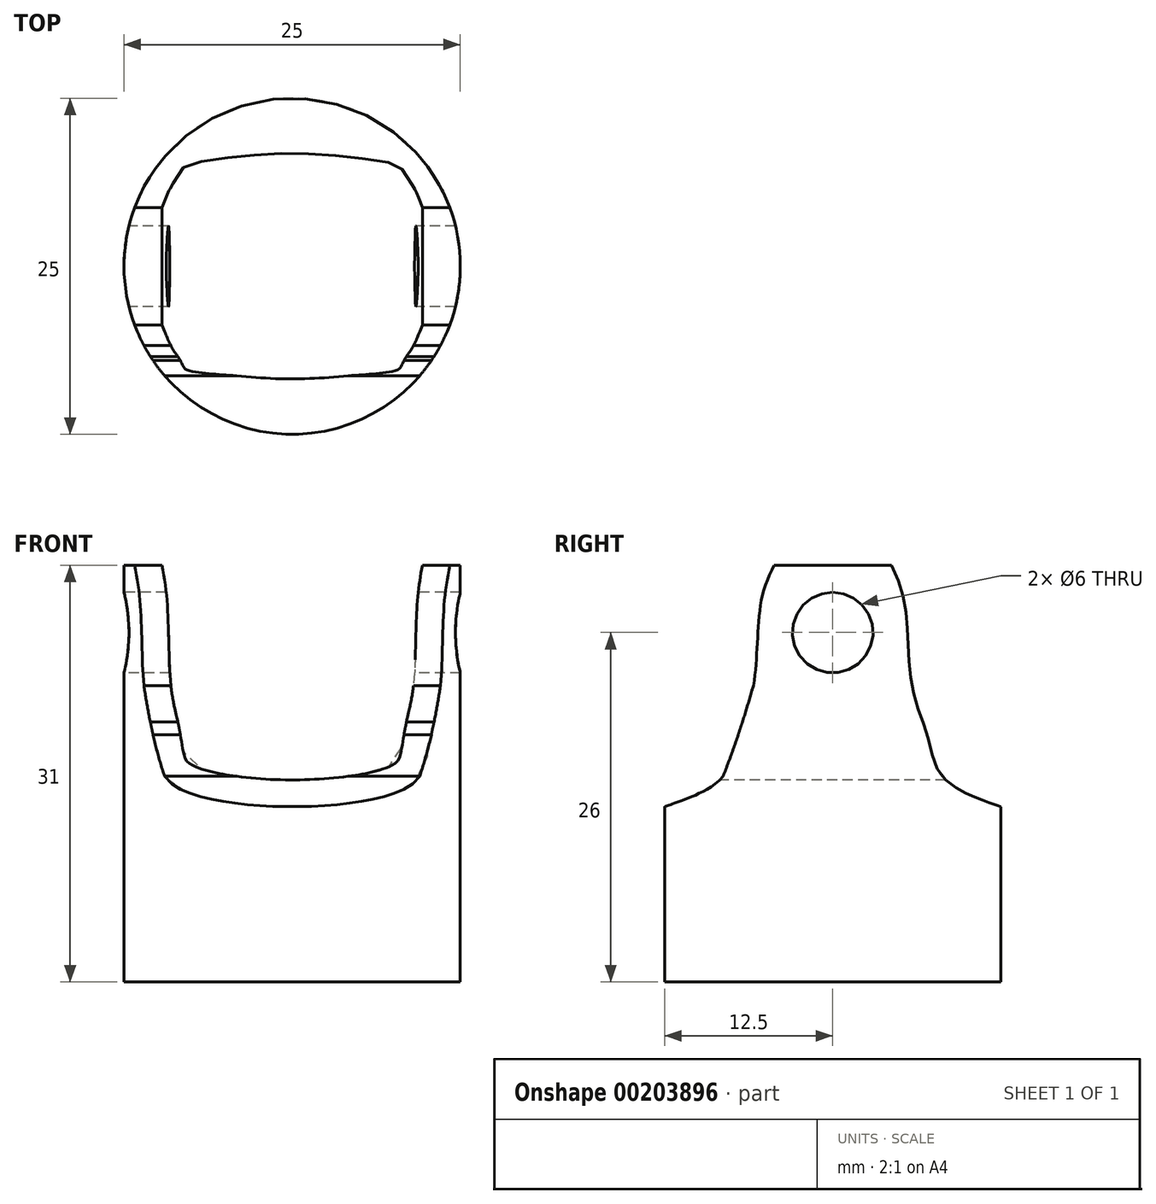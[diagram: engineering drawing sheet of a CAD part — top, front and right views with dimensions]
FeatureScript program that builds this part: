
annotation { "Feature Type Name" : "Feature", "Feature Type Description" : "" }
export const myFeature = defineFeature(function(context is Context, id is Id, definition is map)
    precondition{}
    {
        {
            var Q0;
            Q0=qCreatedBy(makeId("Top.planeOp"),FACE);
            var sketch = newSketch(context, id + "F0", { "sketchPlane" : qUnion([Q0])});
            skCircle(sketch, "E0", {"center": v(0, 0) * mm, "radius": 12.5 * mm});
            skSolve(sketch);
        }
        {
            var Q0;
            Q0=makeQuery(id+"F0.imprint","IMPRINT",FACE,{"disambiguationData":[TD([[makeQuery(id+"F0.imprint","IMPRINT",EDGE,{"derivedFrom":sQuery(id+"F0.wireOp",EDGE,"E0")}),1.0]])]});
            extrude(context, id + "F1", {"entities" : qUnion([Q0]), "depth" : 13 * mm});
        }
        {
            var Q0;
            Q0=makeQuery(id+"F1.opExtrude","CAP_FACE",FACE,{"disambiguationData":[OSD([sQuery(id+"F0.wireOp",EDGE,"E0")])],"isStart":false});
            extrude(context, id + "F2", {"entities" : qUnion([Q0]), "operationType" : NewBodyOperationType.ADD, "depth" : 18 * mm});
        }
        {
            var Q0;
            Q0=qCreatedBy(makeId("Right.planeOp"),FACE);
            var sketch = newSketch(context, id + "F3", { "sketchPlane" : qUnion([Q0])});
            skCircle(sketch, "E1", {"center": v(0, 26) * mm, "radius": 3 * mm});
            skLineSegment(sketch, "E2", {"start": v(-12.63, 13) * mm, "end": v(12.63, 13) * mm});
            skFitSpline(sketch, "E3", {"points": [v(-12.63, 13) * mm, v(-8.14, 15.3) * mm, v(-7.02, 18.39) * mm, v(-5.9, 22.04) * mm, v(-5.33, 28.22) * mm, v(-4.21, 31.3) * mm], "startDerivative": vector(24.86, 8.48) * mm, "endDerivative": vector(7.63, 15.3) * mm});
            skFitSpline(sketch, "E4", {"points": [v(-5.9, 22.04) * mm, v(-7.02, 18.39) * mm, v(-8.14, 15.3) * mm], "startDerivative": vector(-2.12, -7.2) * mm, "endDerivative": vector(-2.37, -6.27) * mm});
            skFitSpline(sketch, "E5.MirrorCS", {"points": [v(12.63, 13) * mm, v(8.14, 15.3) * mm, v(7.02, 18.39) * mm, v(5.9, 22.04) * mm, v(5.33, 28.22) * mm, v(4.21, 31.3) * mm], "startDerivative": vector(-24.86, 8.48) * mm, "endDerivative": vector(-7.63, 15.3) * mm});
            skFitSpline(sketch, "E6.MirrorCS", {"points": [v(12.63, 13) * mm, v(8.14, 15.3) * mm, v(7.02, 18.39) * mm, v(5.9, 22.04) * mm, v(5.33, 28.22) * mm, v(4.21, 31.3) * mm], "startDerivative": vector(-24.86, 8.48) * mm, "endDerivative": vector(-7.63, 15.3) * mm});
            skLineSegment(sketch, "E7", {"start": v(-4.21, 31.3) * mm, "end": v(4.21, 31.3) * mm});
            skLineSegment(sketch, "E8", {"start": v(-12.5, 0) * mm, "end": v(-12.5, 31) * mm});
            skLineSegment(sketch, "E9", {"start": v(12.5, 31) * mm, "end": v(12.5, 0) * mm});
            skLineSegment(sketch, "E10", {"start": v(-12.5, 0) * mm, "end": v(12.5, 0) * mm});
            skSolve(sketch);
        }
        {
            var Q0;
            Q0 = qSketchRegion(id + "F3", true);
            extrude(context, id + "F4", {"entities" : qUnion([Q0]), "operationType" : NewBodyOperationType.INTERSECT, "depth" : 25 * mm, "hasSecondDirection" : true, "secondDirectionOppositeDirection" : true, "secondDirectionDepth" : 25 * mm});
        }
        {
            var Q0;
            Q0=qCreatedBy(makeId("Front.planeOp"),FACE);
            var sketch = newSketch(context, id + "F5", { "sketchPlane" : qUnion([Q0])});
            skFitSpline(sketch, "E11.0", {"points": [v(-11.71, 31) * mm, v(-11.62, 30.5) * mm, v(-11.48, 29.74) * mm, v(-11.34, 28.68) * mm, v(-11.27, 27.86) * mm, v(-11.23, 27.02) * mm, v(-11.2, 25.9) * mm, v(-11.16, 24.47) * mm, v(-11.1, 23.06) * mm, v(-11.02, 21.95) * mm, v(-10.91, 21.12) * mm, v(-10.76, 20.31) * mm, v(-10.59, 19.5) * mm, v(-10.43, 18.84) * mm, v(-10.32, 18.3) * mm, v(-10.23, 17.74) * mm, v(-10.12, 17.03) * mm, v(-9.97, 16.35) * mm, v(-9.8, 15.85) * mm, v(-9.62, 15.5) * mm, v(-9.42, 15.2) * mm, v(-9.1, 14.86) * mm, v(-8.66, 14.52) * mm, v(-8.06, 14.2) * mm, v(-7.4, 13.96) * mm, v(-6.72, 13.76) * mm, v(-6, 13.59) * mm, v(-5.23, 13.44) * mm, v(-4.44, 13.32) * mm, v(-3.63, 13.23) * mm, v(-2.8, 13.15) * mm, v(-1.95, 13.1) * mm, v(-1.1, 13.06) * mm, v(0.05, 13.04) * mm, v(1.19, 13.06) * mm, v(2.33, 13.12) * mm, v(3.45, 13.2) * mm, v(4.53, 13.33) * mm, v(5.56, 13.5) * mm, v(6.32, 13.66) * mm, v(7.03, 13.84) * mm, v(7.7, 14.06) * mm, v(8.33, 14.34) * mm, v(8.81, 14.63) * mm, v(9.16, 14.92) * mm, v(9.4, 15.17) * mm, v(9.6, 15.46) * mm, v(9.77, 15.8) * mm, v(9.9, 16.18) * mm, v(10.05, 16.7) * mm, v(10.18, 17.4) * mm, v(10.3, 18.24) * mm, v(10.48, 19.06) * mm, v(10.67, 19.86) * mm, v(10.83, 20.67) * mm, v(10.97, 21.5) * mm, v(11.06, 22.35) * mm, v(11.1, 23.23) * mm, v(11.15, 24.4) * mm, v(11.19, 25.88) * mm, v(11.24, 27.35) * mm, v(11.32, 28.5) * mm, v(11.46, 29.64) * mm, v(11.61, 30.46) * mm, v(11.71, 31) * mm]});
            skFitSpline(sketch, "E12.0", {"points": [v(-9.75, 31.36) * mm, v(-9.7, 31.11) * mm, v(-9.6, 30.6) * mm, v(-9.47, 29.78) * mm, v(-9.35, 28.9) * mm, v(-9.28, 28) * mm, v(-9.23, 27.1) * mm, v(-9.2, 25.95) * mm, v(-9.16, 24.8) * mm, v(-9.13, 23.7) * mm, v(-9.1, 23.04) * mm, v(-9.06, 22.52) * mm, v(-9.03, 22.15) * mm, v(-8.98, 21.8) * mm, v(-8.91, 21.31) * mm, v(-8.8, 20.72) * mm, v(-8.67, 20.09) * mm, v(-8.54, 19.55) * mm, v(-8.46, 19.19) * mm, v(-8.4, 18.88) * mm, v(-8.36, 18.65) * mm, v(-8.32, 18.42) * mm, v(-8.27, 18.13) * mm, v(-8.21, 17.78) * mm, v(-8.12, 17.27) * mm, v(-8.03, 16.87) * mm, v(-7.94, 16.6) * mm, v(-7.88, 16.49) * mm, v(-7.85, 16.45) * mm, v(-7.82, 16.42) * mm, v(-7.78, 16.37) * mm, v(-7.71, 16.31) * mm, v(-7.6, 16.23) * mm, v(-7.43, 16.14) * mm, v(-7.17, 16.01) * mm, v(-6.78, 15.86) * mm, v(-6.21, 15.7) * mm, v(-5.59, 15.54) * mm, v(-4.9, 15.42) * mm, v(-4.17, 15.3) * mm, v(-3.42, 15.22) * mm, v(-2.65, 15.15) * mm, v(-1.85, 15.1) * mm, v(-1.03, 15.06) * mm, v(0.05, 15.04) * mm, v(1.12, 15.06) * mm, v(2.2, 15.11) * mm, v(3.26, 15.2) * mm, v(4.26, 15.31) * mm, v(5.2, 15.47) * mm, v(5.87, 15.6) * mm, v(6.47, 15.76) * mm, v(7, 15.94) * mm, v(7.36, 16.1) * mm, v(7.57, 16.22) * mm, v(7.7, 16.3) * mm, v(7.79, 16.38) * mm, v(7.84, 16.44) * mm, v(7.87, 16.48) * mm, v(7.93, 16.6) * mm, v(8, 16.77) * mm, v(8.07, 17.04) * mm, v(8.14, 17.36) * mm, v(8.2, 17.73) * mm, v(8.26, 18.07) * mm, v(8.3, 18.37) * mm, v(8.35, 18.6) * mm, v(8.4, 18.83) * mm, v(8.45, 19.13) * mm, v(8.53, 19.5) * mm, v(8.62, 19.9) * mm, v(8.71, 20.3) * mm, v(8.8, 20.67) * mm, v(8.89, 21.16) * mm, v(8.98, 21.75) * mm, v(9.09, 22.76) * mm, v(9.15, 24.16) * mm, v(9.18, 25.63) * mm, v(9.22, 26.83) * mm, v(9.26, 27.6) * mm, v(9.3, 28.22) * mm, v(9.35, 28.85) * mm, v(9.45, 29.64) * mm, v(9.6, 30.54) * mm, v(9.7, 31.1) * mm, v(9.75, 31.36) * mm]});
            skLineSegment(sketch, "E13", {"start": v(11.71, 31) * mm, "end": v(9.75, 31.36) * mm});
            skLineSegment(sketch, "E14", {"start": v(-11.71, 31) * mm, "end": v(-9.75, 31.36) * mm});
            skLineSegment(sketch, "E15", {"start": v(9.75, 31.36) * mm, "end": v(-9.75, 31.36) * mm});
            skSolve(sketch);
        }
        {
            var Q0;
            Q0=makeQuery(id+"F5.imprint","IMPRINT",FACE,{"disambiguationData":[TD([[makeQuery(id+"F5.imprint","IMPRINT",EDGE,{"derivedFrom":sQuery(id+"F5.wireOp",EDGE,"E12.0")}),1.0]])]});
            extrude(context, id + "F6", {"entities" : qUnion([Q0]), "operationType" : NewBodyOperationType.REMOVE, "depth" : 25 * mm, "hasSecondDirection" : true, "secondDirectionOppositeDirection" : true, "secondDirectionDepth" : 25 * mm});
        }
    });
